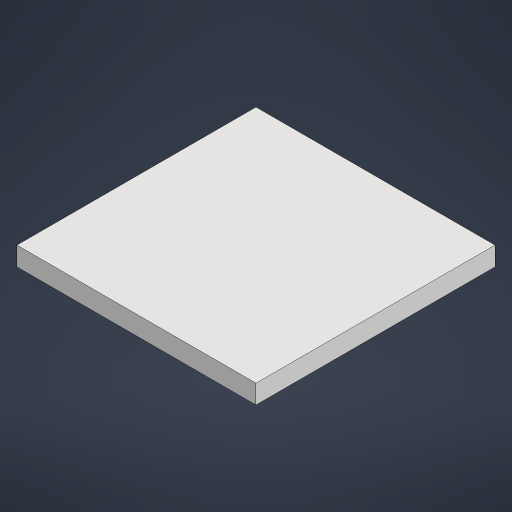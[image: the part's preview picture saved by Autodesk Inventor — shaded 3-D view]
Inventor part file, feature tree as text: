
AUTODESK INVENTOR PART (.ipt)
format: ipt  version: 2023.2 (Build 272271000, 271)  size: 146,944 bytes
history: native  units: in
note: dims shown in document units (in); Inventor stores cm internally (conversion verified against a paired STEP export)
features: extrude x1, sketch x1
ambient origin geometry x8: Origin, YZ Plane, XZ Plane, XY Plane, X Axis, Y Axis, Z Axis, Center Point
bodies: Solid1 (feature_tree)
feature tree (2):
  extrude  "Extrusion1"  Depth=38.0in
  sketch  "Sketch2"  dims[d3=38.0in d4=38.0in d5=3.0in d6=0.0in]
